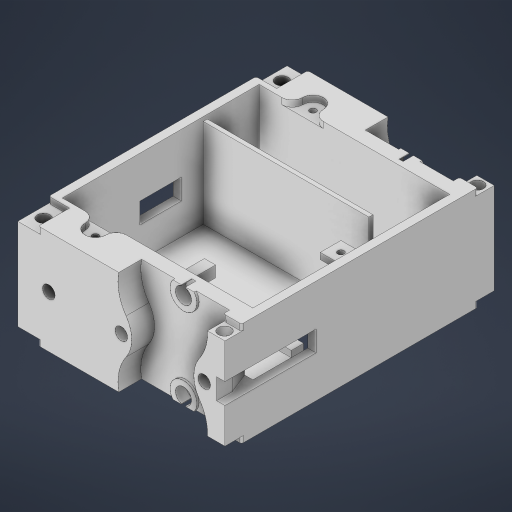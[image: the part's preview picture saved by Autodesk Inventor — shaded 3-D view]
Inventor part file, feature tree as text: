
AUTODESK INVENTOR PART (.ipt)
format: ipt  version: 2024.2 (Build 282272000, 272)  size: 824,832 bytes
history: native  units: in
note: dims shown in document units (in); Inventor stores cm internally (conversion verified against a paired STEP export)
features: extrude x22, sketch x21, projected_geometry x20, mirror x4, plane x2, chamfer x2, fillet x1
ambient origin geometry x8: Origin, YZ Plane, XZ Plane, XY Plane, X Axis, Y Axis, Z Axis, Center Point
bodies: Solid1 (feature_tree)
feature tree (72):
  extrude  "Extrusion1"  Depth=3.937in
  plane  "Work Plane1"
  plane  "Work Plane2"
  extrude  "Extrusion2"  TaperAngle=0.0deg  [1 undecoded]
  extrude  "Extrusion3"  Depth=2.3622in
  extrude  "Extrusion4"  Depth=0.3031in
  mirror  "Mirror1"
  extrude  "Extrusion5"  Depth=1.1811in
  mirror  "Mirror2"
  extrude  "Extrusion6"  Depth=1.6535in
  extrude  "Extrusion7"  Depth=0.0394in
  sketch  "Sketch9"  dims[d18=0.0787in d19=1.6535in]
  extrude  "Extrusion8"  Depth=1.6535in
  extrude  "Extrusion9"  Depth=1.1811in
  mirror  "Mirror3"
  mirror  "Mirror4"
  extrude  "Extrusion10"  Depth=0.8268in
  extrude  "Extrusion11"  Depth=0.0394in
  extrude  "Extrusion12"  Depth=0.7874in
  extrude  "Extrusion13"  Depth=0.3937in
  extrude  "Extrusion15"  Depth=0.1181in
  extrude  "Extrusion16"  Depth=0.315in
  extrude  "Extrusion17"  Depth=0.3937in
  extrude  "Extrusion18"  Depth=0.3937in
  extrude  "Extrusion19"  Depth=0.5906in
  extrude  "Extrusion20"  Depth=0.2362in
  extrude  "Extrusion21"  Depth=0.4331in
  extrude  "Extrusion22"  Depth=0.0394in
  extrude  "Extrusion23"  TaperAngle=0.0deg  [1 undecoded]
  chamfer  "Chamfer1"  Distance=3.622in
  fillet  "Fillet1"  Radius=3.7402in
  chamfer  "Chamfer2"  Distance=1.8701in
  sketch  "Sketch1"  dims[d0=1.9685in d1=3.937in]
  sketch  "Sketch3"  dims[d2=5.1181in d3=0.0in]
  projected_geometry  "Projected Loop1"
  sketch  "Sketch4"  dims[d4=1.1811in d5=2.3622in]
  projected_geometry  "Projected Loop2"
  sketch  "Sketch5"  dims[d6=1.6535in d7=0.3031in]
  projected_geometry  "Projected Loop3"
  sketch  "Sketch6"  dims[d8=0.8268in d11=1.1811in]
  projected_geometry  "Projected Loop4"
  projected_geometry  "Projected Loop5"
  sketch  "Sketch7"  dims[d12=0.5906in d13=0.0in d14=1.6535in]
  projected_geometry  "Projected Loop6"
  sketch  "Sketch8"  dims[d15=0.4331in d16=0.0in d17=0.0394in]
  projected_geometry  "Projected Loop7"
  projected_geometry  "Projected Loop8"
  projected_geometry  "Projected Loop9"
  sketch  "Sketch10"  dims[d20=0.8268in d21=1.1811in]
  projected_geometry  "Projected Loop10"
  sketch  "Sketch11"  dims[d22=0.5118in d23=0.8268in]
  projected_geometry  "Projected Loop11"
  sketch  "Sketch12"  dims[d24=0.0394in d25=0.0in d26=0.2362in]
  projected_geometry  "Projected Loop12"
  sketch  "Sketch13"  dims[d27=1.5748in d28=0.7874in]
  projected_geometry  "Projected Loop13"
  sketch  "Sketch15"  dims[d29=0.5906in d30=0.3937in]
  projected_geometry  "Projected Loop15"
  sketch  "Sketch16"  dims[d31=0.0in d32=0.1181in]
  sketch  "Sketch17"  dims[d33=0.1181in d34=0.315in]
  projected_geometry  "Projected Loop16"
  sketch  "Sketch18"  dims[d35=0.0in d36=0.3937in]
  projected_geometry  "Projected Loop17"
  sketch  "Sketch19"  dims[d37=0.3937in d38=0.1181in]
  projected_geometry  "Projected Loop18"
  sketch  "Sketch20"  dims[d39=0.1181in d40=0.5906in]
  projected_geometry  "Projected Loop19"
  sketch  "Sketch21"  dims[d41=0.0in d42=0.2362in]
  sketch  "Sketch22"  dims[d43=0.2362in d44=0.4331in]
  projected_geometry  "Projected Loop20"
  sketch  "Sketch23"  dims[d45=0.0in d46=0.1969in d47=0.0in d48=3.622in d49=3.7402in d50=1.8701in d51=1.7717in d52=0.0in d53=1.7323in d54=0.3937in d55=0.1969in d56=1.7717in d57=0.0in d58=0.9843in d59=0.9843in d60=0.1181in d61=0.1181in d62=4.1339in d63=2.0669in d64=0.315in d65=0.0in d66=0.3937in d67=0.1181in d68=0.0in d83=0.2126in d84=0.2126in d85=0.2126in d86=0.2126in d87=0.2126in d88=0.2126in d89=0.1181in d90=0.1181in d91=0.1181in d92=1.3622in d93=2.1496in d94=2.1496in d95=0.5512in d96=0.0in d97=0.3937in d98=0.1969in d99=0.3543in d100=0.1181in d101=0.3937in d102=0.0in d103=0.1181in d104=0.2362in d105=0.3937in d106=0.0in d107=0.1181in d108=0.3937in d109=0.0in d110=0.0787in d111=0.6102in d112=1.6929in d113=0.0in d114=0.3937in d115=0.5906in d116=0.0787in d117=1.6929in d118=0.0in d119=0.6299in d120=0.4724in d121=0.315in d122=0.5906in d123=0.0in d124=0.0in d125=0.2362in d126=0.1181in d127=0.1181in d128=0.0984in d129=0.0984in d130=0.1181in d131=0.0in d132=0.7874in d133=0.3937in d134=0.1181in d135=0.0in d136=0.1575in d137=0.3937in d138=45.0deg d139=0.0394in d140=0.2362in d141=0.0787in d142=45.0deg]
  projected_geometry  "Projected Loop21"
note: 2 required parameter values undecoded (feature->parameter linkage not recoverable at this tier; creation-order binding heuristic only, values carry confidence <= 0.55)
